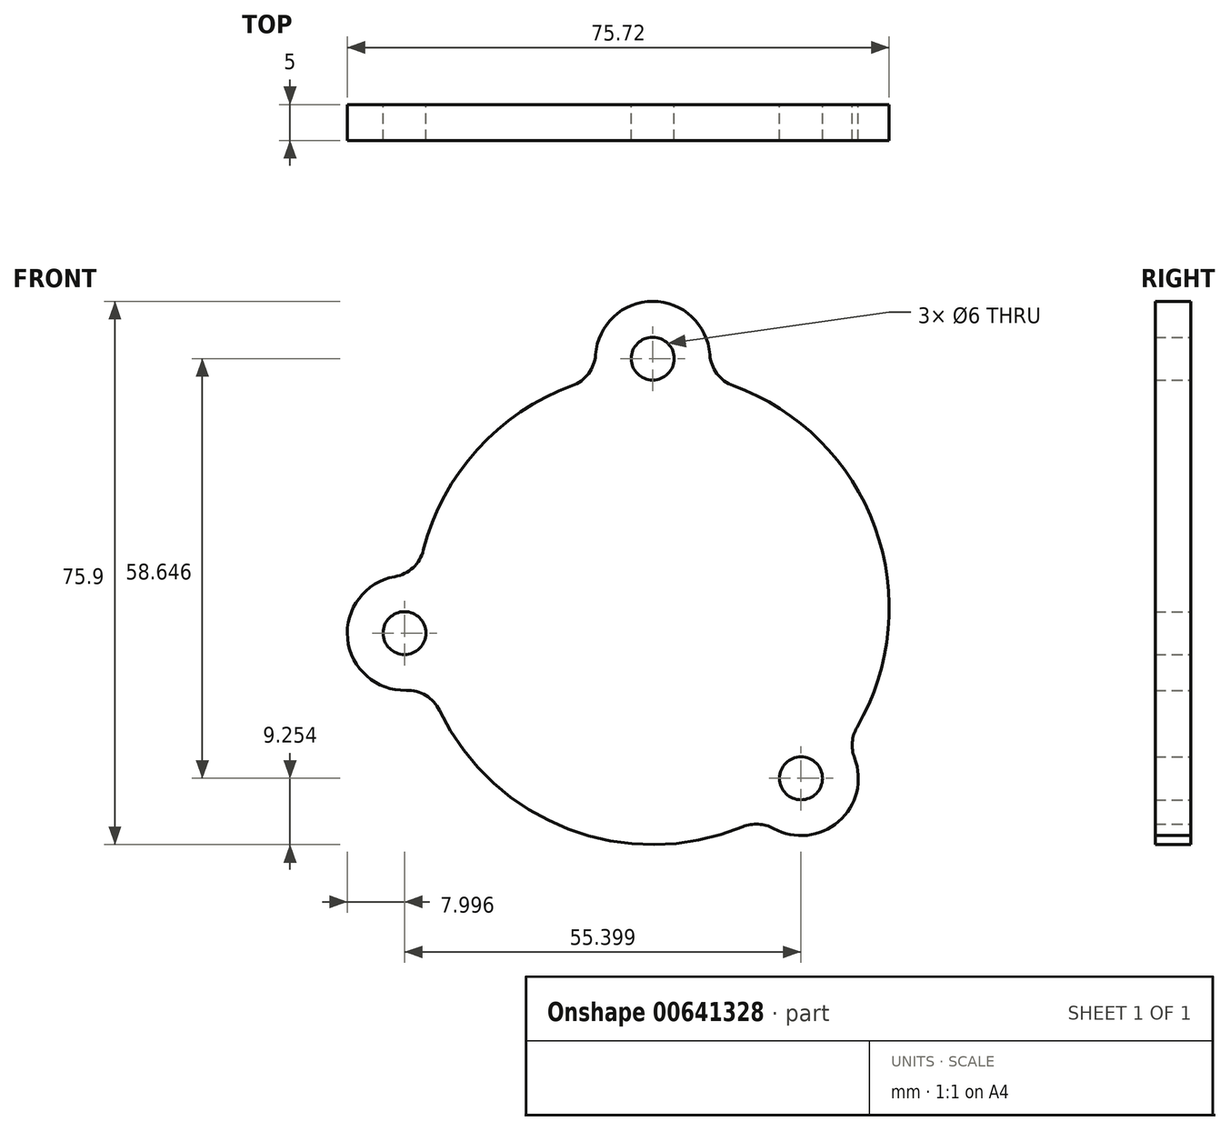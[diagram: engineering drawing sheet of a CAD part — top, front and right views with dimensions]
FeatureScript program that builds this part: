
annotation { "Feature Type Name" : "Feature", "Feature Type Description" : "" }
export const myFeature = defineFeature(function(context is Context, id is Id, definition is map)
    precondition{}
    {
        {
            var Q0;
            Q0=qCreatedBy(makeId("Front.planeOp"),FACE);
            var sketch = newSketch(context, id + "F0", { "sketchPlane" : qUnion([Q0])});
            skCircle(sketch, "E0", {"center": v(0, 34.85) * mm, "radius": 3 * mm});
            skCircle(sketch, "E1", {"center": v(-34.67, -3.5) * mm, "radius": 3 * mm});
            skCircle(sketch, "E2", {"center": v(20.72, -23.8) * mm, "radius": 3 * mm});
            skArc(sketch, "E3", {"start": v(16.87, -30.8) * mm, "mid": v(25.98, -29.83) * mm, "end": v(28.2, -20.94) * mm});
            skArc(sketch, "E4", {"start": v(-29.78, -14.33) * mm, "mid": v(-11.83, -30.86) * mm, "end": v(12.57, -30.57) * mm});
            skArc(sketch, "E5", {"start": v(7.98, 35.42) * mm, "mid": v(0, 42.85) * mm, "end": v(-7.98, 35.42) * mm});
            skArc(sketch, "E6", {"start": v(-36.04, 4.38) * mm, "mid": v(-42.63, -4.3) * mm, "end": v(-34.44, -11.5) * mm});
            skArc(sketch, "E7.trimOffspring", {"start": v(28.55, -16.64) * mm, "mid": v(31.07, 11.26) * mm, "end": v(11.26, 31.07) * mm});
            skArc(sketch, "E8.trimOffspring", {"start": v(-11.26, 31.07) * mm, "mid": v(-24.51, 22.16) * mm, "end": v(-32.04, 8.09) * mm});
            skArc(sketch, "E9.filletArc", {"start": v(-36.04, 4.38) * mm, "mid": v(-33.5, 5.64) * mm, "end": v(-32.04, 8.09) * mm});
            skArc(sketch, "E10.filletArc", {"start": v(-11.26, 31.07) * mm, "mid": v(-8.98, 32.76) * mm, "end": v(-7.98, 35.42) * mm});
            skArc(sketch, "E11.filletArc", {"start": v(7.98, 35.42) * mm, "mid": v(8.98, 32.76) * mm, "end": v(11.26, 31.07) * mm});
            skArc(sketch, "E12.filletArc", {"start": v(28.55, -16.64) * mm, "mid": v(27.89, -18.75) * mm, "end": v(28.2, -20.94) * mm});
            skPoint(sketch, "E13.visualSharp", {"position": v(15.04, -29.43) * mm});
            skArc(sketch, "E13.filletArc", {"start": v(16.87, -30.8) * mm, "mid": v(14.75, -30.2) * mm, "end": v(12.57, -30.57) * mm});
            skArc(sketch, "E14.filletArc", {"start": v(-29.78, -14.33) * mm, "mid": v(-31.69, -12.22) * mm, "end": v(-34.44, -11.5) * mm});
            skSolve(sketch);
        }
        {
            var Q0;
            Q0 = qSketchRegion(id + "F0", true);
            extrude(context, id + "F1", {"entities" : qUnion([Q0]), "depth" : 5 * mm, "offsetDistance" : 25 * mm});
        }
    });
